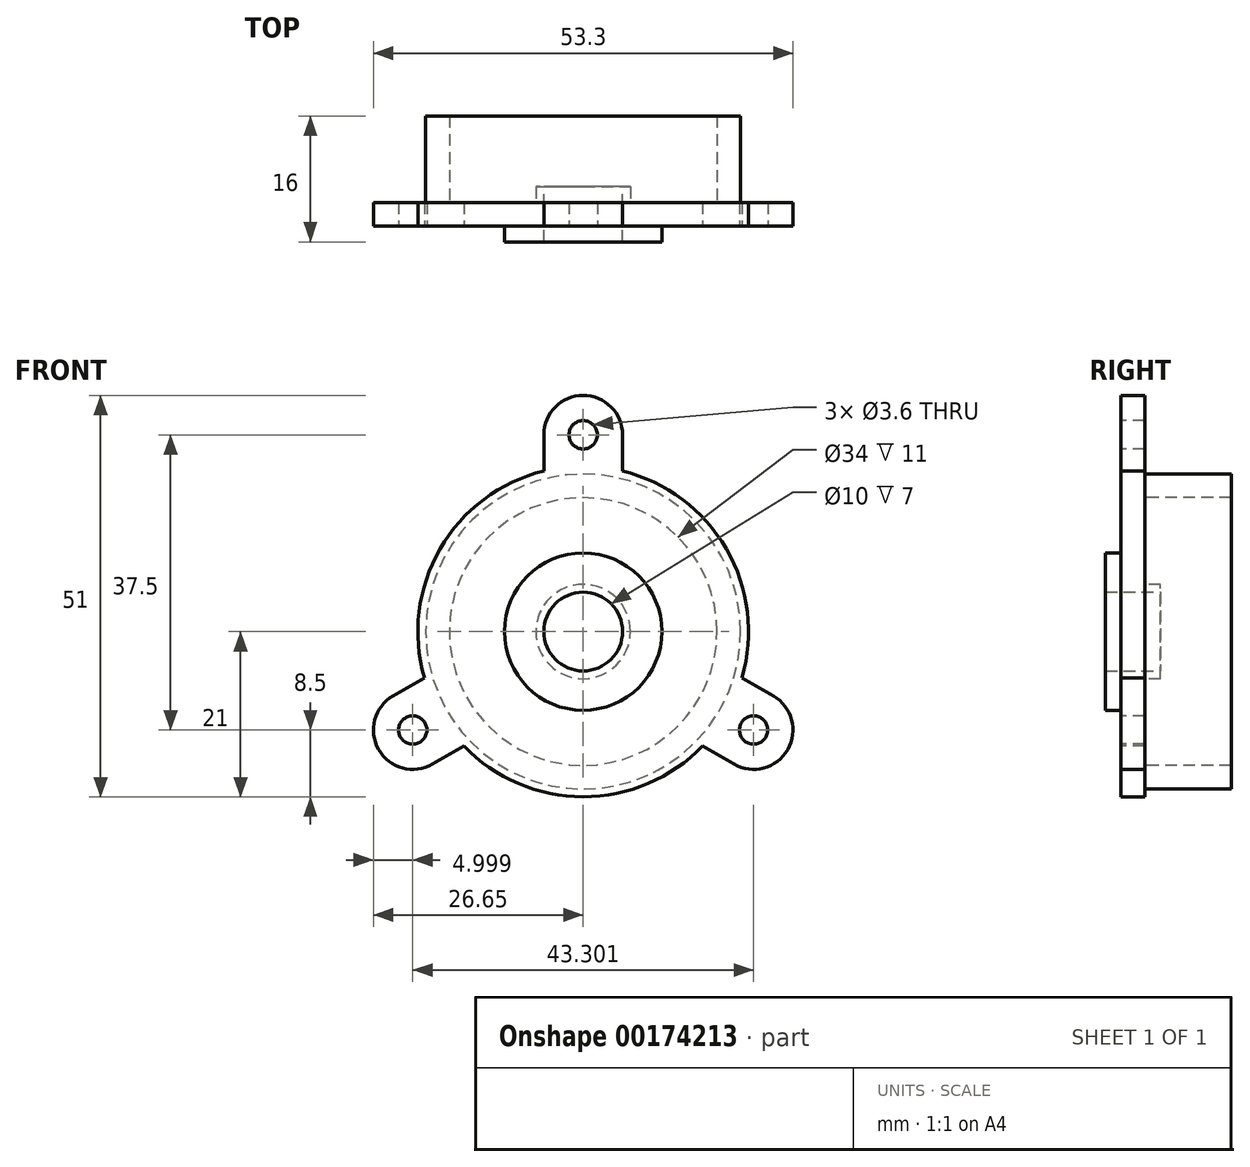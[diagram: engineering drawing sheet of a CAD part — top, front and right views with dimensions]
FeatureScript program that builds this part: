
annotation { "Feature Type Name" : "Feature", "Feature Type Description" : "" }
export const myFeature = defineFeature(function(context is Context, id is Id, definition is map)
    precondition{}
    {
        {
            var Q0;
            Q0=qCreatedBy(makeId("Front.planeOp"),FACE);
            var sketch = newSketch(context, id + "F0", { "sketchPlane" : qUnion([Q0])});
            skCircle(sketch, "E0", {"center": v(0, 0) * mm, "radius": 21 * mm});
            skSolve(sketch);
        }
        {
            var Q0;
            Q0=makeQuery(id+"F0.imprint","IMPRINT",FACE,{"disambiguationData":[TD([[makeQuery(id+"F0.imprint","IMPRINT",EDGE,{"derivedFrom":sQuery(id+"F0.wireOp",EDGE,"E0")}),1.0]])]});
            extrude(context, id + "F1", {"entities" : qUnion([Q0]), "depth" : 3 * mm});
        }
        {
            var Q0;
            Q0=makeQuery(id+"F1.opExtrude","CAP_FACE",FACE,{"disambiguationData":[OSD([sQuery(id+"F0.wireOp",EDGE,"E0")])],"isStart":false});
            var sketch = newSketch(context, id + "F2", { "sketchPlane" : qUnion([Q0])});
            skArc(sketch, "E1", {"start": v(5, 25) * mm, "mid": v(0, 30) * mm, "end": v(-5, 25) * mm});
            skLineSegment(sketch, "E2", {"start": v(-5, 25) * mm, "end": v(-5, 20.4) * mm});
            skLineSegment(sketch, "E3", {"start": v(5, 25) * mm, "end": v(5, 20.4) * mm});
            skPoint(sketch, "E4.start.orphan", {"position": v(-1.1, 25) * mm});
            skCircle(sketch, "E5", {"center": v(0, 25) * mm, "radius": 3.35 * mm});
            skCircle(sketch, "E6", {"center": v(0, 25) * mm, "radius": 1.8 * mm});
            skArc(sketch, "E7.1.0", {"start": v(-24.15, -8.17) * mm, "mid": v(-25.98, -15) * mm, "end": v(-19.15, -16.83) * mm});
            skLineSegment(sketch, "E7.1.1", {"start": v(-19.15, -16.83) * mm, "end": v(-15.16, -14.53) * mm});
            skCircle(sketch, "E7.1.2", {"center": v(-21.65, -12.5) * mm, "radius": 3.35 * mm});
            skLineSegment(sketch, "E7.1.3", {"start": v(-24.15, -8.17) * mm, "end": v(-20.16, -5.87) * mm});
            skCircle(sketch, "E7.1.4", {"center": v(-21.65, -12.5) * mm, "radius": 1.8 * mm});
            skArc(sketch, "E7.2.0", {"start": v(19.15, -16.83) * mm, "mid": v(25.98, -15) * mm, "end": v(24.15, -8.17) * mm});
            skLineSegment(sketch, "E7.2.1", {"start": v(24.15, -8.17) * mm, "end": v(20.16, -5.87) * mm});
            skCircle(sketch, "E7.2.2", {"center": v(21.65, -12.5) * mm, "radius": 3.35 * mm});
            skLineSegment(sketch, "E7.2.3", {"start": v(19.15, -16.83) * mm, "end": v(15.16, -14.53) * mm});
            skCircle(sketch, "E7.2.4", {"center": v(21.65, -12.5) * mm, "radius": 1.8 * mm});
            skPoint(sketch, "E7.center", {"position": v(0, 0) * mm});
            skSolve(sketch);
        }
        {
            var Q0;
            Q0 = qSketchRegion(id + "F2", true);
            var Q1;
            Q1=makeQuery(id+"F2.imprint","IMPRINT",FACE,{"disambiguationData":[TD([[makeQuery(id+"F2.imprint","IMPRINT",EDGE,{"derivedFrom":sQuery(id+"F2.wireOp",EDGE,"E1")}),1.0]])]});
            var Q2;
            Q2=makeQuery(id+"F2.imprint","IMPRINT",FACE,{"disambiguationData":[TD([[makeQuery(id+"F2.imprint","IMPRINT",EDGE,{"derivedFrom":sQuery(id+"F2.wireOp",EDGE,"E7.2.0")}),1.0]])]});
            var Q3;
            Q3=makeQuery(id+"F2.imprint","IMPRINT",FACE,{"disambiguationData":[TD([[makeQuery(id+"F2.imprint","IMPRINT",EDGE,{"derivedFrom":sQuery(id+"F2.wireOp",EDGE,"E7.1.0")}),1.0]])]});
            extrude(context, id + "F3", {"entities" : qUnion([Q0, Q1, Q2, Q3]), "operationType" : NewBodyOperationType.ADD, "oppositeDirection" : true, "depth" : 3 * mm});
        }
        {
            var Q0;
            {var subQ0=sQuery(id+"F0.wireOp",EDGE,"E0");Q0=makeQuery(id+"F3.boolean.opBoolean","MERGE",FACE,{"derivedFrom":[makeQuery(id+"F1.opExtrude","CAP_FACE",FACE,{"disambiguationData":[OSD([subQ0])],"isStart":true}),makeQuery(id+"F3.opExtrude","CAP_FACE",FACE,{"disambiguationData":[OSD([subQ0,sQuery(id+"F2.wireOp",EDGE,"E1"),sQuery(id+"F2.wireOp",EDGE,"E2"),sQuery(id+"F2.wireOp",EDGE,"E3"),sQuery(id+"F2.wireOp",EDGE,"E6")])],"isStart":false}),makeQuery(id+"F3.opExtrude","CAP_FACE",FACE,{"disambiguationData":[OSD([subQ0,sQuery(id+"F2.wireOp",EDGE,"E7.1.0"),sQuery(id+"F2.wireOp",EDGE,"E7.1.1"),sQuery(id+"F2.wireOp",EDGE,"E7.1.3"),sQuery(id+"F2.wireOp",EDGE,"E7.1.4")])],"isStart":false}),makeQuery(id+"F3.opExtrude","CAP_FACE",FACE,{"disambiguationData":[OSD([subQ0,sQuery(id+"F2.wireOp",EDGE,"E7.2.0"),sQuery(id+"F2.wireOp",EDGE,"E7.2.1"),sQuery(id+"F2.wireOp",EDGE,"E7.2.3"),sQuery(id+"F2.wireOp",EDGE,"E7.2.4")])],"isStart":false})]});}
            var sketch = newSketch(context, id + "F4", { "sketchPlane" : qUnion([Q0])});
            skCircle(sketch, "E8", {"center": v(0, 0) * mm, "radius": 20 * mm});
            skCircle(sketch, "E9", {"center": v(0, 0) * mm, "radius": 17 * mm});
            skSolve(sketch);
        }
        {
            var Q0;
            Q0 = qSketchRegion(id + "F4", true);
            extrude(context, id + "F5", {"entities" : qUnion([Q0]), "operationType" : NewBodyOperationType.ADD, "depth" : 11 * mm});
        }
        {
            var Q0;
            Q0=qCreatedBy(makeId("Front.planeOp"),FACE);
            var sketch = newSketch(context, id + "F6", { "sketchPlane" : qUnion([Q0])});
            skCircle(sketch, "E10", {"center": v(0, 0) * mm, "radius": 5 * mm});
            skCircle(sketch, "E11", {"center": v(0, 0) * mm, "radius": 6 * mm});
            skSolve(sketch);
        }
        {
            var Q0;
            Q0=makeQuery(id+"F6.imprint","IMPRINT",FACE,{"disambiguationData":[TD([[makeQuery(id+"F6.imprint","IMPRINT",EDGE,{"derivedFrom":sQuery(id+"F6.wireOp",EDGE,"E10")}),1.0]])]});
            var Q1;
            Q1=makeQuery(id+"F6.imprint","IMPRINT",FACE,{"disambiguationData":[TD([[makeQuery(id+"F6.imprint","IMPRINT",EDGE,{"derivedFrom":sQuery(id+"F6.wireOp",EDGE,"E10")}),-1.0]])]});
            extrude(context, id + "F7", {"entities" : qUnion([Q0, Q1]), "operationType" : NewBodyOperationType.ADD, "oppositeDirection" : true, "depth" : 2 * mm});
        }
        {
            var Q0;
            {var subQ0=sQuery(id+"F0.wireOp",EDGE,"E0");Q0=makeQuery(id+"F3.boolean.opBoolean","MERGE",FACE,{"derivedFrom":[makeQuery(id+"F1.opExtrude","CAP_FACE",FACE,{"disambiguationData":[OSD([subQ0])],"isStart":false}),makeQuery(id+"F3.opExtrude","CAP_FACE",FACE,{"disambiguationData":[OSD([subQ0,sQuery(id+"F2.wireOp",EDGE,"E1"),sQuery(id+"F2.wireOp",EDGE,"E2"),sQuery(id+"F2.wireOp",EDGE,"E3"),sQuery(id+"F2.wireOp",EDGE,"E6")])],"isStart":true}),makeQuery(id+"F3.opExtrude","CAP_FACE",FACE,{"disambiguationData":[OSD([subQ0,sQuery(id+"F2.wireOp",EDGE,"E7.1.0"),sQuery(id+"F2.wireOp",EDGE,"E7.1.1"),sQuery(id+"F2.wireOp",EDGE,"E7.1.3"),sQuery(id+"F2.wireOp",EDGE,"E7.1.4")])],"isStart":true}),makeQuery(id+"F3.opExtrude","CAP_FACE",FACE,{"disambiguationData":[OSD([subQ0,sQuery(id+"F2.wireOp",EDGE,"E7.2.0"),sQuery(id+"F2.wireOp",EDGE,"E7.2.1"),sQuery(id+"F2.wireOp",EDGE,"E7.2.3"),sQuery(id+"F2.wireOp",EDGE,"E7.2.4")])],"isStart":true})]});}
            var sketch = newSketch(context, id + "F8", { "sketchPlane" : qUnion([Q0])});
            skCircle(sketch, "E12", {"center": v(0, 0) * mm, "radius": 10 * mm});
            skSolve(sketch);
        }
        {
            var Q0;
            Q0=makeQuery(id+"F8.imprint","IMPRINT",FACE,{"disambiguationData":[TD([[makeQuery(id+"F8.imprint","IMPRINT",EDGE,{"derivedFrom":sQuery(id+"F8.wireOp",EDGE,"E12")}),1.0]])]});
            extrude(context, id + "F9", {"entities" : qUnion([Q0]), "operationType" : NewBodyOperationType.ADD, "depth" : 2 * mm});
        }
        {
            var Q0;
            Q0=makeQuery(id+"F7.opExtrude","CAP_FACE",FACE,{"disambiguationData":[OSD([sQuery(id+"F6.wireOp",EDGE,"E11")])],"isStart":false});
            var sketch = newSketch(context, id + "F10", { "sketchPlane" : qUnion([Q0])});
            skCircle(sketch, "E13", {"center": v(0, 0) * mm, "radius": 5 * mm});
            skSolve(sketch);
        }
        {
            var Q0;
            Q0 = qSketchRegion(id + "F10", true);
            extrude(context, id + "F11", {"entities" : qUnion([Q0]), "operationType" : NewBodyOperationType.REMOVE, "oppositeDirection" : true, "depth" : 46.6 * mm});
        }
    });
